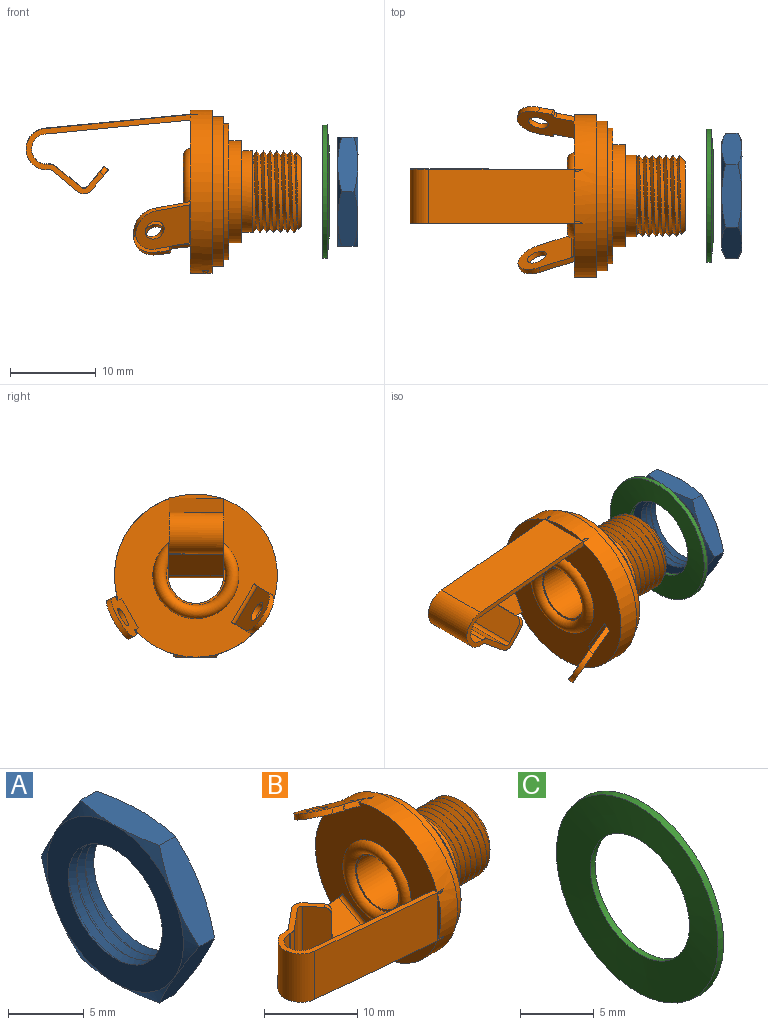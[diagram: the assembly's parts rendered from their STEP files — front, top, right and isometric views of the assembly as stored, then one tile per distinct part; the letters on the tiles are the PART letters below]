
ASSEMBLY  parts=3 mates=2
PART A: 26 faces, bbox 2.9x15.2x15.2 mm
  f0: cone r=4.36mm half-angle=43.8deg, axis (-1,0,0), area 15.8mm2, adj f1,f7
  f1: cone r=4.78mm half-angle=43.8deg, axis (1,0,0), area 15.8mm2, adj f0,f2
  f2: cone r=4.36mm half-angle=43.8deg, axis (-1,0,0), area 15.8mm2, adj f1,f4
  f3: cone r=6.33mm half-angle=65deg, axis (1,0,0), area 3.8mm2, adj f14,f15,f25
  f4: cone r=4.78mm half-angle=43.8deg, axis (1,0,0), area 15.8mm2, adj f2,f5
  f5: cone r=4.36mm half-angle=43.8deg, axis (-1,0,0), area 15.8mm2, adj f4,f6
  f6: cone r=4.78mm half-angle=43.8deg, axis (1,0,0), area 15.8mm2, adj f5,f25
  f7: plane 12.7x12.7mm, normal (1,0,0), area 66.4mm2, adj f0,f8,f9,f10,f11,f12,f13
  f8: cone r=7.36mm half-angle=65deg, axis (-1,0,0), area 3.8mm2, adj f7,f14,f15
  f9: cone r=7.36mm half-angle=65deg, axis (-1,0,0), area 3.8mm2, adj f7,f15,f16
  f10: cone r=7.36mm half-angle=65deg, axis (-1,0,0), area 3.8mm2, adj f7,f16,f17
  f11: cone r=7.36mm half-angle=65deg, axis (-1,0,0), area 3.8mm2, adj f7,f17,f18
  f12: cone r=7.36mm half-angle=65deg, axis (-1,0,0), area 3.8mm2, adj f7,f18,f19
  f13: cone r=7.36mm half-angle=65deg, axis (-1,0,0), area 3.8mm2, adj f7,f14,f19
  f14: plane 6.91x4.23mm, normal (0,0.87,0.5), area 15.1mm2, adj f3,f8,f13,f15,f19,f20
  f15: plane 6.91x4.23mm, normal (0,0.87,-0.5), area 15.1mm2, adj f3,f8,f9,f14,f16,f21
  f16: plane 7.9x2.95mm, normal (0,0,-1), area 15.1mm2, adj f9,f10,f15,f17,f21,f22
  f17: plane 6.91x4.23mm, normal (0,-0.87,-0.5), area 15.1mm2, adj f10,f11,f16,f18,f22,f23
  f18: plane 6.91x4.23mm, normal (0,-0.87,0.5), area 15.1mm2, adj f11,f12,f17,f19,f23,f24
  f19: plane 7.9x2.95mm, normal (0,0,1), area 15.1mm2, adj f12,f13,f14,f18,f20,f24
  f20: cone r=6.33mm half-angle=65deg, axis (1,0,0), area 3.8mm2, adj f14,f19,f25
  f21: cone r=6.33mm half-angle=65deg, axis (1,0,0), area 3.8mm2, adj f15,f16,f25
  f22: cone r=6.33mm half-angle=65deg, axis (1,0,0), area 3.8mm2, adj f16,f17,f25
  f23: cone r=6.33mm half-angle=65deg, axis (1,0,0), area 3.8mm2, adj f17,f18,f25
  f24: cone r=6.33mm half-angle=65deg, axis (1,0,0), area 3.8mm2, adj f18,f19,f25
  f25: plane 12.7x12.7mm, normal (-1,0,0), area 66.4mm2, adj f3,f6,f20,f21,f22,f23,f24
PART B: 88 faces, bbox 32.4x19.2x20 mm
  f0: cylinder r=1.15mm len=6.35mm, axis (0,0,-1), area 11.5mm2, adj f17,f22,f52,f57
  f1: cylinder r=0.51mm len=6.35mm, axis (0,0,-1), area 5.1mm2, adj f21,f24,f52,f57
  f2: cylinder r=2.42mm len=6.35mm, axis (0,0,-1), area 48.3mm2, adj f25,f52,f55,f57
  f3: cylinder r=1.18mm len=2.44mm, axis (0.34,0.47,-0.81), area 4.7mm2, adj f38,f39
  f4: cylinder r=1.78mm len=6.35mm, axis (0,0,-1), area 35.5mm2, adj f27,f40,f52,f57
  f5: cylinder r=1.18mm len=2.45mm, axis (-0.22,-0.49,-0.85), area 4.8mm2, adj f41,f49
  f6: cylinder r=9.53mm len=19.05mm, axis (1,0,0), area 149.7mm2, adj f48,f49,f50,f51,f52,f53,f54,f55
  f7: cylinder r=8.74mm len=17.48mm, axis (1,0,0), area 71.1mm2, adj f79,f80
  f8: cylinder r=7.94mm len=15.88mm, axis (1,0,0), area 31.7mm2, adj f80,f81
  f9: cylinder r=5.95mm len=11.91mm, axis (-1,0,0), area 55.1mm2, adj f81,f82
  f10: torus R=4.24mm, axis (1,0,0), area 65.9mm2, adj f83,f84
  f11: cylinder r=3.23mm len=12.35mm, axis (-1,0,0), area 250.8mm2, adj f12,f84
  f12: cone r=3.61mm half-angle=30deg, axis (1,0,0), area 15.7mm2, adj f11,f85
  f13: cone r=4mm half-angle=45deg, axis (-1,0,0), area 18.2mm2, adj f14,f85,f86,f87
  f14: cone r=4mm half-angle=45deg, axis (-1,0,0), area 0.9mm2, adj f13,f86,f87
  f15: cylinder r=4.76mm len=9.53mm, axis (1,0,0), area 38mm2, adj f16,f82
  f16: plane 9.53x9.53mm, normal (1,0,0), area 7.1mm2, adj f15,f86,f87
  f17: plane 6.35x2.37mm, normal (0.77,0.64,0), area 19.2mm2, adj f0,f18,f19,f20,f52,f57
  f18: cylinder r=0.79mm len=1.02mm, axis (-0.77,-0.64,0), area 0.8mm2, adj f17,f19,f21,f57
  f19: plane 4.76x0.5mm, normal (0.64,-0.77,0), area 3.1mm2, adj f17,f18,f20,f21
  f20: cylinder r=0.79mm len=1.02mm, axis (-0.77,-0.64,0), area 0.8mm2, adj f17,f19,f21,f52
  f21: plane 6.35x2.37mm, normal (-0.77,-0.64,0), area 19.2mm2, adj f1,f18,f19,f20,f52,f57
  f22: plane 6.35x2.97mm, normal (-0.64,0.77,0), area 24.5mm2, adj f0,f23,f52,f57
  f23: cylinder r=0.51mm len=6.35mm, axis (0,0,-1), area 2.5mm2, adj f22,f25,f52,f57
  f24: plane 6.35x2.97mm, normal (0.64,-0.77,0), area 24.5mm2, adj f1,f26,f52,f57
  f25: plane 6.35x0.05mm, normal (0.1,1,0), area 0.3mm2, adj f2,f23,f52,f57
  f26: cylinder r=1.15mm len=6.35mm, axis (0,0,-1), area 5.7mm2, adj f24,f27,f52,f57
  f27: plane 6.35x0.05mm, normal (-0.1,-1,0), area 0.3mm2, adj f4,f26,f52,f57
  f28: cylinder r=2.58mm len=4.81mm, axis (-0.34,-0.47,0.81), area 5.1mm2, adj f38,f39,f42,f44
  f29: cylinder r=0.25mm len=0.63mm, axis (-0.22,-0.49,-0.85), area 0.3mm2, adj f30,f41,f49,f51
  f30: plane 0.59x0.39mm, normal (0.98,-0.11,-0.19), area 0.1mm2, adj f29,f31,f41,f49
  f31: cylinder r=0.25mm len=0.63mm, axis (0.22,0.49,0.85), area 0.3mm2, adj f30,f32,f41,f49
  f32: plane 1.64x0.83mm, normal (0,0.87,-0.5), area 1mm2, adj f31,f33,f41,f49
  f33: cylinder r=2.58mm len=4.8mm, axis (-0.22,-0.49,-0.85), area 5.2mm2, adj f32,f34,f41,f49
  f34: plane 1.64x0.83mm, normal (0,-0.87,0.5), area 1mm2, adj f33,f35,f41,f49
  f35: cylinder r=0.25mm len=0.72mm, axis (0.22,0.49,0.85), area 0.3mm2, adj f34,f36,f41,f49
  f36: plane 0.59x0.39mm, normal (0.98,-0.11,-0.19), area 0.1mm2, adj f35,f37,f41,f49
  f37: cylinder r=0.25mm len=0.72mm, axis (-0.22,-0.49,-0.85), area 0.3mm2, adj f36,f41,f49,f58
  f38: plane 6.25x5.21mm, normal (0.34,0.47,-0.81), area 27.1mm2, adj f3,f28,f42,f43,f44
  f39: plane 6.25x5.21mm, normal (-0.34,-0.47,0.81), area 27.1mm2, adj f3,f28,f42,f44,f46
  f40: plane 16.94x6.35mm, normal (0.1,1,0), area 108.1mm2, adj f4,f52,f57,f83
  f41: plane 6.68x4.65mm, normal (-0.22,-0.49,-0.85), area 25.1mm2, adj f5,f29,f30,f31,f32,f33,f34,f35
  f42: plane 4.19x2.01mm, normal (0,0.87,0.5), area 2.8mm2, adj f28,f38,f39,f43,f46,f47,f83
  f43: cylinder r=1.14mm len=4.49mm, axis (0,-0.87,-0.5), area 0.7mm2, adj f38,f42,f44,f83
  f44: plane 4.19x2.01mm, normal (0,-0.87,-0.5), area 2.8mm2, adj f28,f38,f39,f43,f45,f46,f83
  f45: bspline ~0.17x0.15mm, area 0mm2, adj f44,f46,f83
  f46: cylinder r=0.51mm len=4.77mm, axis (0,-0.87,-0.5), area 3.2mm2, adj f39,f42,f44,f45,f47,f83
  f47: bspline ~0.21x0.12mm, area 0mm2, adj f42,f46,f83
  f48: cylinder r=0.25mm len=0.11mm, axis (-0.22,-0.49,-0.85), area 0mm2, adj f6,f49,f58
  f49: plane 7.59x4.65mm, normal (0.22,0.49,0.85), area 26.2mm2, adj f5,f6,f29,f30,f31,f32,f33,f34
  f50: cylinder r=0.25mm len=0.11mm, axis (-0.22,-0.49,-0.85), area 0mm2, adj f6,f49,f51
  f51: plane 3.12x0.96mm, normal (0,0.87,-0.5), area 1.5mm2, adj f6,f29,f41,f49,f50,f83
  f52: plane 20.16x9.3mm, normal (0,0,-1), area 20.5mm2, adj f0,f1,f2,f4,f6,f17,f20,f21
  f53: cylinder r=2.23mm len=0.81mm, axis (0,0,-1), area 0.1mm2, adj f6,f52,f55
  f54: plane 6.02x0.49mm, normal (-1,0,0), area 2mm2, adj f6,f55
  f55: plane 17.16x6.35mm, normal (-0.1,-1,0), area 108.5mm2, adj f2,f6,f52,f53,f54,f56,f57
  f56: cylinder r=2.23mm len=0.81mm, axis (0,0,-1), area 0.1mm2, adj f6,f55,f57
  f57: plane 20.16x9.3mm, normal (0,0,1), area 20.5mm2, adj f0,f1,f2,f4,f6,f17,f18,f21
  f58: plane 3.12x0.96mm, normal (0,-0.87,0.5), area 1.5mm2, adj f6,f37,f41,f48,f49,f83
  f59: plane 4.36x0.58mm, normal (-0.42,0.91,0), area 1.4mm2, adj f6,f60,f61,f63,f65,f66
  f60: plane 0.45x0.11mm, normal (-0.91,-0.42,0), area 0mm2, adj f6,f59,f61
  f61: cylinder r=0.4mm len=0.75mm, axis (-0.91,-0.42,0), area 0.3mm2, adj f6,f59,f60,f62,f63
  f62: plane 0.13x0.05mm, normal (0,0,1), area 0mm2, adj f6,f61,f63
  f63: plane 5.16x0.42mm, normal (0.91,0.42,0), area 0.9mm2, adj f6,f59,f61,f62,f64,f65
  f64: plane 0.13x0.05mm, normal (0,0,-1), area 0mm2, adj f6,f63,f65
  f65: cylinder r=0.4mm len=0.75mm, axis (-0.91,-0.42,0), area 0.3mm2, adj f6,f59,f63,f64,f66
  f66: plane 0.45x0.11mm, normal (-0.91,-0.42,0), area 0mm2, adj f6,f59,f65
  f67: cylinder r=0.25mm len=0.28mm, axis (0.22,0.49,0.85), area 0mm2, adj f6,f68,f70,f72
  f68: plane 0.23x0.05mm, normal (0,-0.87,0.5), area 0mm2, adj f6,f67,f70
  f69: cylinder r=1.15mm len=0.02mm, axis (0,-0.87,0.5), area 0mm2, adj f6,f70
  f70: plane 0.52x0.47mm, normal (0.22,0.49,0.85), area 0.1mm2, adj f6,f67,f68,f69,f71,f72
  f71: cylinder r=0.25mm len=0.11mm, axis (-0.22,-0.49,-0.85), area 0mm2, adj f6,f70,f72
  f72: plane 0.1x0.06mm, normal (-0.98,0.11,0.19), area 0mm2, adj f6,f67,f70,f71
  f73: cylinder r=0.25mm len=0.1mm, axis (-0.22,-0.49,-0.85), area 0mm2, adj f6,f74,f78
  f74: plane 0.52x0.39mm, normal (0.22,0.49,0.85), area 0.1mm2, adj f6,f73,f75,f76,f77,f78
  f75: cylinder r=1.15mm len=0.02mm, axis (0,-0.87,0.5), area 0mm2, adj f6,f74
  f76: plane 0.23x0.05mm, normal (0,0.87,-0.5), area 0mm2, adj f6,f74,f77
  f77: cylinder r=0.25mm len=0.26mm, axis (0.22,0.49,0.85), area 0mm2, adj f6,f74,f76,f78
  f78: plane 0.09x0.08mm, normal (-0.98,0.11,0.19), area 0mm2, adj f6,f73,f74,f77
  f79: plane 19.05x19.05mm, normal (1,0,0), area 45.2mm2, adj f6,f7
  f80: plane 17.48x17.48mm, normal (1,0,0), area 41.9mm2, adj f7,f8
  f81: plane 15.88x15.88mm, normal (1,0,0), area 86.6mm2, adj f8,f9
  f82: plane 11.91x11.91mm, normal (1,0,0), area 40.1mm2, adj f9,f15
  f83: plane 19.08x18.53mm, normal (-1,0,0), area 192mm2, adj f6,f10,f40,f41,f42,f43,f44,f45
  f84: plane 6.91x6.91mm, normal (-1,0,0), area 4.7mm2, adj f10,f11
  f85: plane 8.03x8.03mm, normal (1,0,0), area 9.9mm2, adj f12,f13
  f86: bspline ~9.79x9.79mm, area 118.4mm2, adj f13,f14,f16,f87
  f87: bspline ~9.76x9.76mm, area 118.4mm2, adj f13,f14,f16,f86
PART C: 4 faces, bbox 0.8x15.6x15.6 mm
  f0: cone r=7.87mm half-angle=85deg, axis (-1,0,0), area 119.5mm2, adj f1,f2
  f1: cone r=4.76mm half-angle=5deg, axis (1,0,0), area 15.3mm2, adj f0,f3
  f2: cone r=7.76mm half-angle=5deg, axis (1,0,0), area 24.9mm2, adj f0,f3
  f3: cone r=7.83mm half-angle=85deg, axis (-1,0,0), area 118.7mm2, adj f1,f2
PLACE A rot(axis=(-1,0,0),0deg) t=(4.34,0.6,-8.1)mm
PLACE B rot(axis=(-1,0,0),89.6deg) t=(10.94,0.6,-8.1)mm
PLACE C rot(axis=(1,0,0),0.4deg) t=(7.78,0.6,-8.1)mm
MATE cylindrical C.f0 <-> B.f12  axis (1,0,0) through (20.74,0.6,-8.1)mm
MATE cylindrical C.f0 <-> A.f8  axis (-1,0,0) through (21.24,0.6,-8.1)mm
